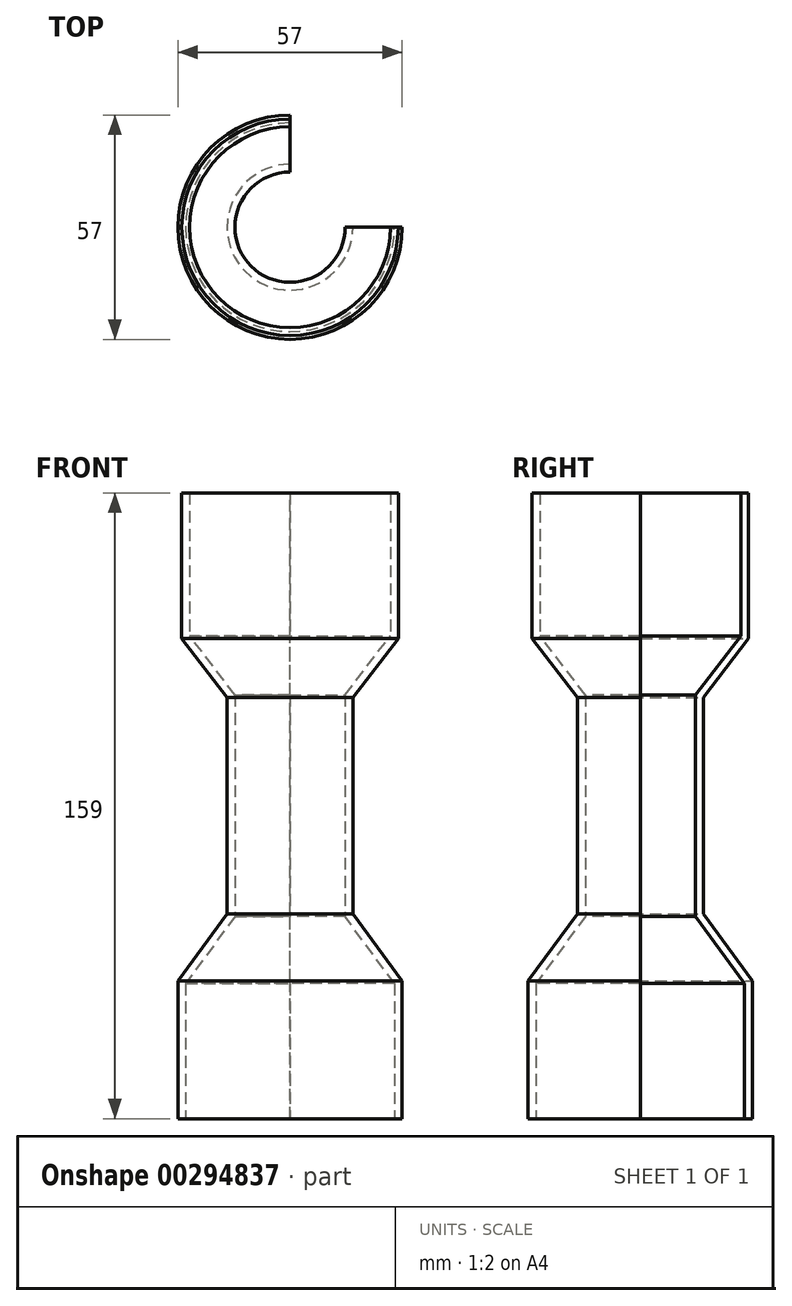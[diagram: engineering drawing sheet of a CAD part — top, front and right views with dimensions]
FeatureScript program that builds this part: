
annotation { "Feature Type Name" : "Feature", "Feature Type Description" : "" }
export const myFeature = defineFeature(function(context is Context, id is Id, definition is map)
    precondition{}
    {
        {
            var Q0;
            Q0=qCreatedBy(makeId("Top.planeOp"),FACE);
            cPlane(context, id + "F0", {"entities" : qUnion([Q0]), "cplaneType" : CPlaneType.OFFSET, "offset" : 35 * mm, "width" : 150 * mm, "height" : 150 * mm});
        }
        {
            var Q0;
            Q0=qCreatedBy(makeId("Top.planeOp"),FACE);
            cPlane(context, id + "F1", {"entities" : qUnion([Q0]), "cplaneType" : CPlaneType.OFFSET, "offset" : 52 * mm, "width" : 150 * mm, "height" : 150 * mm});
        }
        {
            var Q0;
            Q0=qCreatedBy(makeId("Top.planeOp"),FACE);
            cPlane(context, id + "F2", {"entities" : qUnion([Q0]), "cplaneType" : CPlaneType.OFFSET, "offset" : 107 * mm, "width" : 150 * mm, "height" : 150 * mm});
        }
        {
            var Q0;
            Q0=qCreatedBy(id+"F2.planeOp",FACE);
            cPlane(context, id + "F3", {"entities" : qUnion([Q0]), "cplaneType" : CPlaneType.OFFSET, "offset" : 15 * mm, "width" : 150 * mm, "height" : 150 * mm});
        }
        {
            var Q0;
            Q0=qCreatedBy(id+"F3.planeOp",FACE);
            cPlane(context, id + "F4", {"entities" : qUnion([Q0]), "cplaneType" : CPlaneType.OFFSET, "offset" : 37 * mm, "width" : 150 * mm, "height" : 150 * mm});
        }
        {
            var Q0;
            Q0=qCreatedBy(makeId("Right.planeOp"),FACE);
            var sketch = newSketch(context, id + "F5", { "sketchPlane" : qUnion([Q0])});
            skLineSegment(sketch, "E0", {"start": v(28.5, 0) * mm, "end": v(0, 0) * mm});
            skLineSegment(sketch, "E1", {"start": v(0, 0) * mm, "end": v(0, 159) * mm});
            skLineSegment(sketch, "E2", {"start": v(28.5, 0) * mm, "end": v(28.5, 35) * mm});
            skLineSegment(sketch, "E3", {"start": v(28.5, 35) * mm, "end": v(16, 52) * mm});
            skLineSegment(sketch, "E4", {"start": v(16, 52) * mm, "end": v(16, 107) * mm});
            skLineSegment(sketch, "E5", {"start": v(16, 107) * mm, "end": v(27.5, 122) * mm});
            skLineSegment(sketch, "E6", {"start": v(27.5, 122) * mm, "end": v(27.5, 159) * mm});
            skLineSegment(sketch, "E7", {"start": v(27.5, 159) * mm, "end": v(0, 159) * mm});
            skSolve(sketch);
        }
        {
            var Q0;
            Q0=makeQuery(id+"F5.imprint","IMPRINT",FACE,{"disambiguationData":[TD([[makeQuery(id+"F5.imprint","IMPRINT",EDGE,{"derivedFrom":sQuery(id+"F5.wireOp",EDGE,"E0")}),-1.0]])]});
            var Q1;
            Q1=sQuery(id+"F5.wireOp",EDGE,"E1");
            revolve(context, id + "F6", {"entities" : qUnion([Q0]), "axis" : qUnion([Q1]), "revolveType" : RevolveType.ONE_DIRECTION, "angle" : 270 * degree});
        }
        {
            var Q0;
            Q0=makeQuery(id+"F6.opRevolve","CAP_FACE",FACE,{"disambiguationData":[OSD([sQuery(id+"F5.wireOp",EDGE,"E0"),sQuery(id+"F5.wireOp",EDGE,"E1"),sQuery(id+"F5.wireOp",EDGE,"E2"),sQuery(id+"F5.wireOp",EDGE,"E3"),sQuery(id+"F5.wireOp",EDGE,"E4"),sQuery(id+"F5.wireOp",EDGE,"E5"),sQuery(id+"F5.wireOp",EDGE,"E6"),sQuery(id+"F5.wireOp",EDGE,"E7")])],"isStart":true});
            var Q1;
            Q1=makeQuery(id+"F6.opRevolve","SWEPT_FACE",FACE,{"disambiguationData":[OSD([sQuery(id+"F5.wireOp",EDGE,"E7")])]});
            var Q2;
            Q2=makeQuery(id+"F6.opRevolve","CAP_FACE",FACE,{"disambiguationData":[OSD([sQuery(id+"F5.wireOp",EDGE,"E0"),sQuery(id+"F5.wireOp",EDGE,"E1"),sQuery(id+"F5.wireOp",EDGE,"E2"),sQuery(id+"F5.wireOp",EDGE,"E3"),sQuery(id+"F5.wireOp",EDGE,"E4"),sQuery(id+"F5.wireOp",EDGE,"E5"),sQuery(id+"F5.wireOp",EDGE,"E6"),sQuery(id+"F5.wireOp",EDGE,"E7")])],"isStart":false});
            var Q3;
            Q3=makeQuery(id+"F6.opRevolve","SWEPT_FACE",FACE,{"disambiguationData":[OSD([sQuery(id+"F5.wireOp",EDGE,"E0")])]});
            shell(context, id + "F7", {"entities" : qUnion([Q0, Q1, Q2, Q3]), "thickness" : 2 * mm});
        }
        {
            var Q0;
            Q0=qCreatedBy(makeId("Front.planeOp"),FACE);
            cPlane(context, id + "F8", {"entities" : qUnion([Q0]), "cplaneType" : CPlaneType.OFFSET, "offset" : 40 * mm, "width" : 150 * mm, "height" : 150 * mm});
        }
    });
